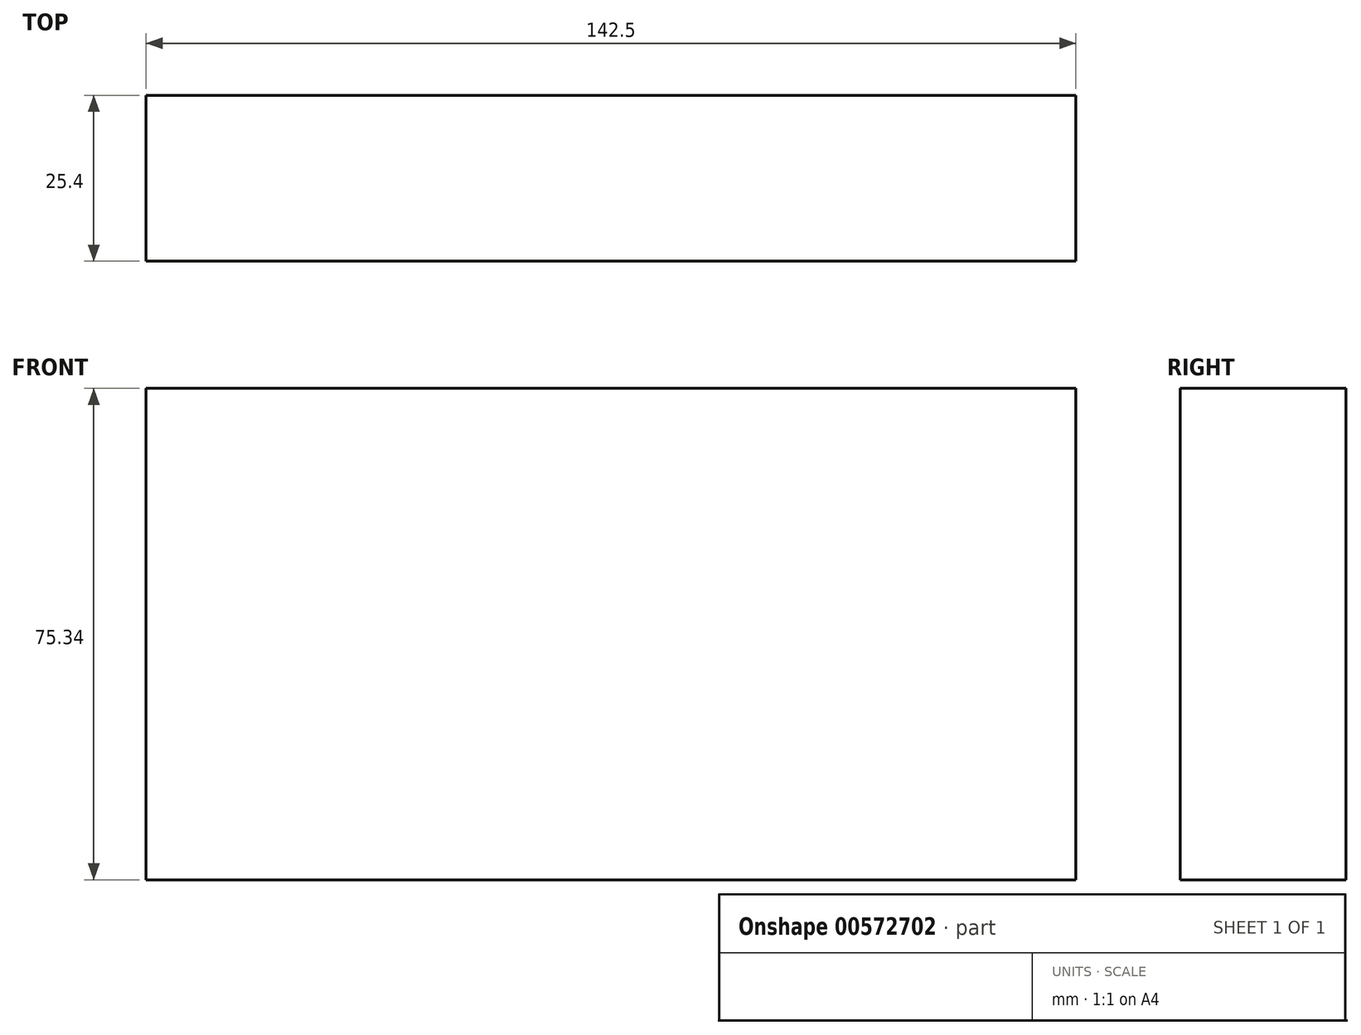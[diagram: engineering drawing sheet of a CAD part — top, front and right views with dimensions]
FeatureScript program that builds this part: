
annotation { "Feature Type Name" : "Feature", "Feature Type Description" : "" }
export const myFeature = defineFeature(function(context is Context, id is Id, definition is map)
    precondition{}
    {
        {
            var Q0;
            Q0=qCreatedBy(makeId("Front.planeOp"),FACE);
            var sketch = newSketch(context, id + "F0", { "sketchPlane" : qUnion([Q0])});
            skLineSegment(sketch, "E0.bottom", {"start": v(71.25, -37.67) * mm, "end": v(-71.25, -37.67) * mm});
            skLineSegment(sketch, "E0.top", {"start": v(71.25, 37.67) * mm, "end": v(-71.25, 37.67) * mm});
            skLineSegment(sketch, "E0.left", {"start": v(71.25, -37.67) * mm, "end": v(71.25, 37.67) * mm});
            skLineSegment(sketch, "E0.right", {"start": v(-71.25, -37.67) * mm, "end": v(-71.25, 37.67) * mm});
            skPoint(sketch, "E0.middle", {"position": v(0, 0) * mm});
            skSolve(sketch);
        }
        {
            var Q0;
            Q0=makeQuery(id+"F0.imprint","IMPRINT",FACE,{"disambiguationData":[TD([[makeQuery(id+"F0.imprint","IMPRINT",EDGE,{"derivedFrom":sQuery(id+"F0.wireOp",EDGE,"E0.bottom")}),-1.0]])]});
            extrude(context, id + "F1", {"entities" : qUnion([Q0]), "depth" : 25.4 * mm, "offsetDistance" : 25.4 * mm});
        }
    });
